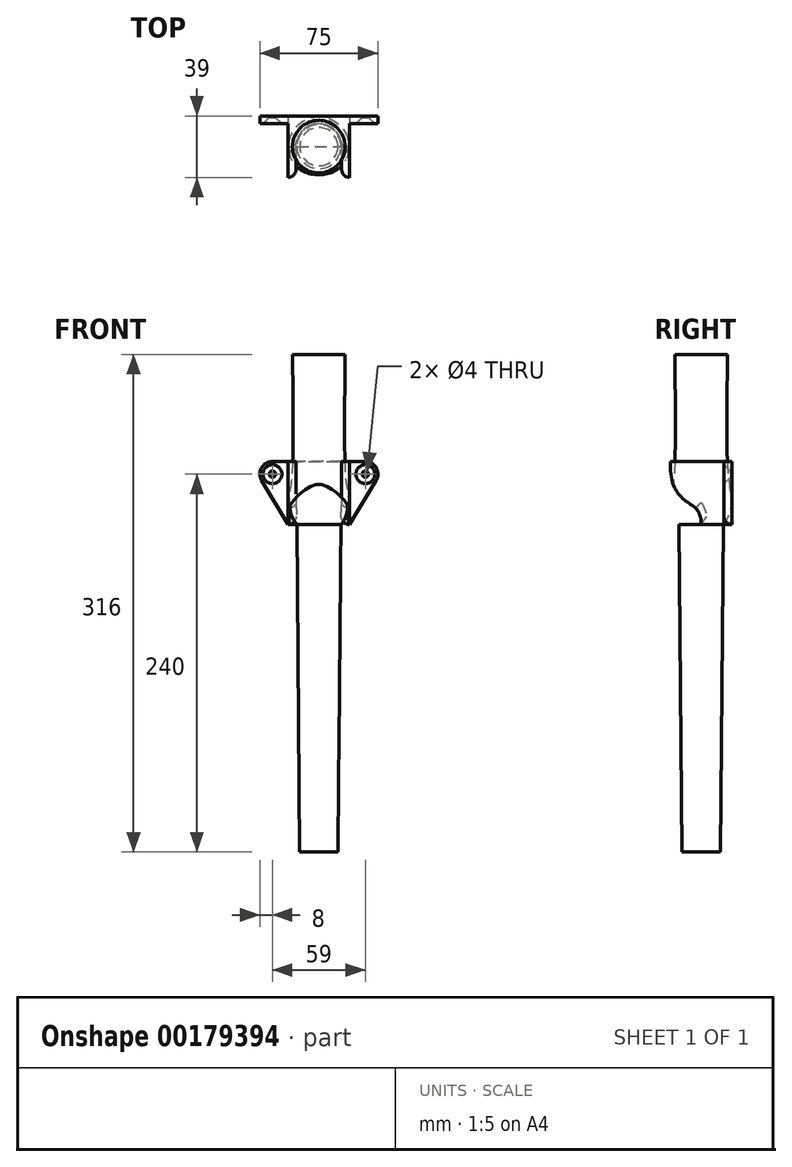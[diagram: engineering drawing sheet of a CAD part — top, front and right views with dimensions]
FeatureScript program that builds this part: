
annotation { "Feature Type Name" : "Feature", "Feature Type Description" : "" }
export const myFeature = defineFeature(function(context is Context, id is Id, definition is map)
    precondition{}
    {
        {
            assignVariable(context, id + "F0", {"name" : "Thickness", "anyValue" : 5});
        }
        {
            var Q0;
            Q0=qCreatedBy(makeId("Front.planeOp"),FACE);
            var sketch = newSketch(context, id + "F1", { "sketchPlane" : qUnion([Q0])});
            skLineSegment(sketch, "E0", {"start": v(-14, 0) * mm, "end": v(-12.15, -208) * mm});
            skLineSegment(sketch, "E1", {"start": v(-12.15, -208) * mm, "end": v(0, -208) * mm});
            skFitSpline(sketch, "E2", {"points": [v(-14, 0) * mm, v(-19, 12.42) * mm, v(-17.34, 29.52) * mm, v(-16.75, 108) * mm], "startDerivative": vector(-36.66, 38.6) * mm, "endDerivative": vector(-1.57, 152.15) * mm});
            skLineSegment(sketch, "E3", {"start": v(-16.75, 108) * mm, "end": v(0, 108) * mm});
            skLineSegment(sketch, "E4", {"start": v(0, 108) * mm, "end": v(0, -208) * mm});
            skSolve(sketch);
        }
        {
            var Q0;
            Q0=makeQuery(id+"F1.imprint","IMPRINT",FACE,{"disambiguationData":[TD([[makeQuery(id+"F1.imprint","IMPRINT",EDGE,{"derivedFrom":sQuery(id+"F1.wireOp",EDGE,"E0")}),1.0]])]});
            var Q1;
            Q1=sQuery(id+"F1.wireOp",EDGE,"E4");
            revolve(context, id + "F2", {"entities" : qUnion([Q0]), "axis" : qUnion([Q1]), "revolveType" : RevolveType.FULL});
        }
        {
            var Q0;
            Q0=qCreatedBy(makeId("Top.planeOp"),FACE);
            var sketch = newSketch(context, id + "F3", { "sketchPlane" : qUnion([Q0])});
            skArc(sketch, "E5.0", {"start": v(14.5, 0) * mm, "mid": v(0, 14.5) * mm, "end": v(-14.5, 0) * mm});
            skLineSegment(sketch, "E6", {"start": v(-14.5, 0) * mm, "end": v(-14.5, -19.5) * mm});
            skLineSegment(sketch, "E7", {"start": v(14.5, 0) * mm, "end": v(14.5, -19.5) * mm});
            skLineSegment(sketch, "E8.bottom", {"start": v(-19.5, 19.5) * mm, "end": v(19.5, 19.5) * mm});
            skLineSegment(sketch, "E8.top", {"start": v(-19.5, -19.5) * mm, "end": v(-14.5, -19.5) * mm});
            skLineSegment(sketch, "E8.left", {"start": v(-19.5, 19.5) * mm, "end": v(-19.5, -19.5) * mm});
            skLineSegment(sketch, "E8.right", {"start": v(19.5, 19.5) * mm, "end": v(19.5, -19.5) * mm});
            skLineSegment(sketch, "E9.trimOffspring", {"start": v(14.5, -19.5) * mm, "end": v(19.5, -19.5) * mm});
            skSolve(sketch);
        }
        {
            var Q0;
            {var subQ1=sQuery(id+"F3.wireOp",EDGE,"E6");Q0=makeQuery(id+"F3.imprint","IMPRINT",FACE,{"disambiguationData":[TD([[makeQuery(id+"F3.imprint","IMPRINT",EDGE,{"derivedFrom":subQ1}),-1.0]])]});}
            extrude(context, id + "F4", {"entities" : qUnion([Q0]), "depth" : 40 * mm});
        }
        {
            var Q0;
            Q0=makeQuery(id+"F4.opExtrude","SWEPT_FACE",FACE,{"disambiguationData":[OSD([sQuery(id+"F3.wireOp",EDGE,"E8.right")])]});
            var sketch = newSketch(context, id + "F5", { "sketchPlane" : qUnion([Q0])});
            skFitSpline(sketch, "E10", {"points": [v(-19.5, 40) * mm, v(-14.81, 19.97) * mm, v(-7.62, 13.46) * mm, v(0, 0) * mm], "startDerivative": vector(0, -89.38) * mm, "endDerivative": vector(0, -80.8) * mm});
            skLineSegment(sketch, "E11", {"start": v(-19.5, 40) * mm, "end": v(-19.5, 0) * mm});
            skLineSegment(sketch, "E12", {"start": v(-19.5, 0) * mm, "end": v(0, 0) * mm});
            skSolve(sketch);
        }
        {
            var Q0;
            Q0=makeQuery(id+"F5.imprint","IMPRINT",FACE,{"disambiguationData":[TD([[makeQuery(id+"F5.imprint","IMPRINT",EDGE,{"derivedFrom":sQuery(id+"F5.wireOp",EDGE,"E10")}),-1.0]])]});
            extrude(context, id + "F6", {"entities" : qUnion([Q0]), "operationType" : NewBodyOperationType.REMOVE, "endBound" : BoundingType.THROUGH_ALL, "oppositeDirection" : true, "depth" : 25 * mm});
        }
        {
            var Q0;
            Q0=makeQuery(id+"F4.opExtrude","SWEPT_FACE",FACE,{"disambiguationData":[OSD([sQuery(id+"F3.wireOp",EDGE,"E8.bottom")])]});
            var sketch = newSketch(context, id + "F7", { "sketchPlane" : qUnion([Q0])});
            skLineSegment(sketch, "E13", {"start": v(-19.5, 40) * mm, "end": v(-29.5, 40) * mm});
            skCircle(sketch, "E14", {"center": v(-29.5, 32) * mm, "radius": 2 * mm});
            skLineSegment(sketch, "E15.MirrorCS", {"start": v(19.5, 40) * mm, "end": v(29.5, 40) * mm});
            skCircle(sketch, "E16.MirrorC", {"center": v(29.5, 32) * mm, "radius": 2 * mm});
            skLineSegment(sketch, "E17", {"start": v(-19.5, 40) * mm, "end": v(-19.5, 0) * mm});
            skLineSegment(sketch, "E18.MirrorCS", {"start": v(19.5, 40) * mm, "end": v(19.5, 0) * mm});
            skLineSegment(sketch, "E19", {"start": v(-19.5, 0) * mm, "end": v(-36.35, 27.86) * mm});
            skArc(sketch, "E20", {"start": v(-29.5, 40) * mm, "mid": v(-36.47, 35.93) * mm, "end": v(-36.35, 27.86) * mm});
            skArc(sketch, "E21.MirrorCS", {"start": v(29.5, 40) * mm, "mid": v(36.47, 35.93) * mm, "end": v(36.35, 27.86) * mm});
            skLineSegment(sketch, "E22.MirrorCS", {"start": v(19.5, 0) * mm, "end": v(36.35, 27.86) * mm});
            skSolve(sketch);
        }
        {
            var Q0;
            Q0 = qSketchRegion(id + "F7", true);
            extrude(context, id + "F8", {"entities" : qUnion([Q0]), "operationType" : NewBodyOperationType.ADD, "oppositeDirection" : true, "depth" : (getVariable(context, 'Thickness')) * mm});
        }
        {
            var Q0;
            Q0=makeQuery(id+"F8.opExtrude","CAP_EDGE",EDGE,{"disambiguationData":[OSD([sQuery(id+"F7.wireOp",EDGE,"E18.MirrorCS")])],"isStart":false});
            var Q1;
            Q1=makeQuery(id+"F8.opExtrude","CAP_EDGE",EDGE,{"disambiguationData":[OSD([sQuery(id+"F7.wireOp",EDGE,"E17")])],"isStart":false});
            var Q2;
            Q2=makeQuery(id+"F6.boolean.opBoolean","INTERSECT",EDGE,{"derivedFrom":[makeQuery(id+"F4.opExtrude","SWEPT_FACE",FACE,{"disambiguationData":[OSD([sQuery(id+"F3.wireOp",EDGE,"E6")])]}),makeQuery(id+"F6.opExtrude","SWEPT_FACE",FACE,{"disambiguationData":[OSD([sQuery(id+"F5.wireOp",EDGE,"E10")])]})]});
            var Q3;
            Q3=makeQuery(id+"F6.boolean.opBoolean","INTERSECT",EDGE,{"derivedFrom":[makeQuery(id+"F4.opExtrude","SWEPT_FACE",FACE,{"disambiguationData":[OSD([sQuery(id+"F3.wireOp",EDGE,"E7")])]}),makeQuery(id+"F6.opExtrude","SWEPT_FACE",FACE,{"disambiguationData":[OSD([sQuery(id+"F5.wireOp",EDGE,"E10")])]})]});
            var Q4;
            Q4=makeQuery(id+"F4.opExtrude","CAP_EDGE",EDGE,{"disambiguationData":[OSD([sQuery(id+"F3.wireOp",EDGE,"E5.0")])],"isStart":true});
            fillet(context, id + "F9", {"entities" : qUnion([Q0, Q1, Q2, Q3, Q4]), "radius" : 5 * mm, "tangentPropagation" : true, "allowEdgeOverflow" : false});
        }
        {
            var Q0;
            Q0=makeQuery(id+"F8.opExtrude","CAP_EDGE",EDGE,{"disambiguationData":[OSD([sQuery(id+"F7.wireOp",EDGE,"E14")])],"isStart":false});
            var Q1;
            Q1=makeQuery(id+"F8.opExtrude","CAP_EDGE",EDGE,{"disambiguationData":[OSD([sQuery(id+"F7.wireOp",EDGE,"E16.MirrorC")])],"isStart":false});
            chamfer(context, id + "F10", {"entities" : qUnion([Q0, Q1]), "width" : 4 * mm, "tangentPropagation" : true});
        }
    });
